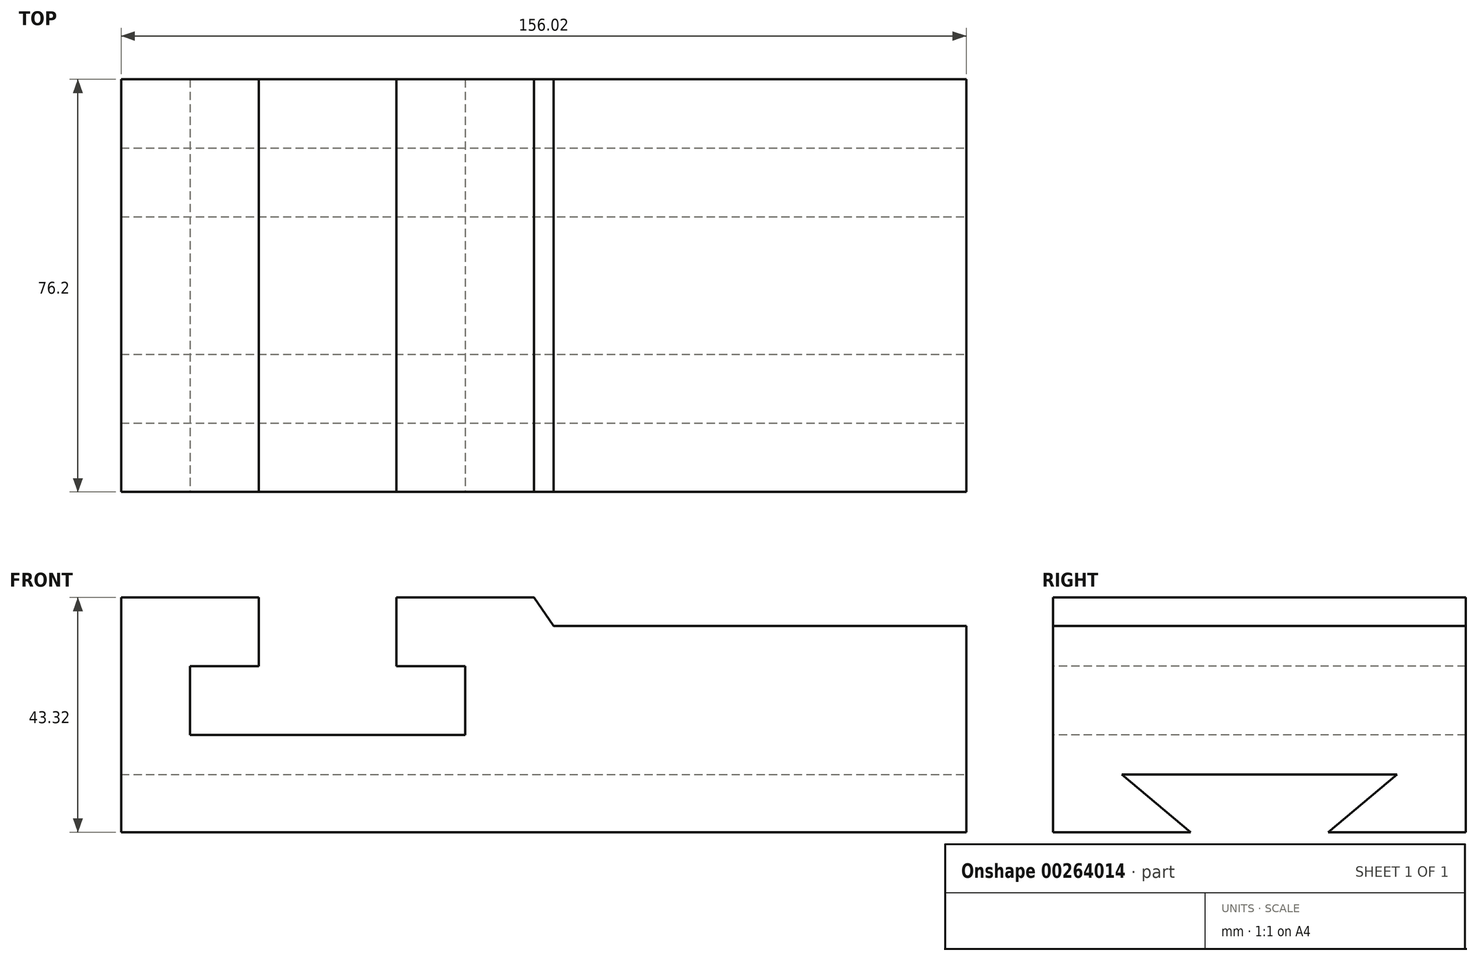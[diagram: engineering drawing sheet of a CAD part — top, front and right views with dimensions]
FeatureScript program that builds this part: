
annotation { "Feature Type Name" : "Feature", "Feature Type Description" : "" }
export const myFeature = defineFeature(function(context is Context, id is Id, definition is map)
    precondition{}
    {
        {
            var Q0;
            Q0=qCreatedBy(makeId("Front.planeOp"),FACE);
            var sketch = newSketch(context, id + "F0", { "sketchPlane" : qUnion([Q0])});
            skLineSegment(sketch, "E0", {"start": v(0, 0) * mm, "end": v(-76.2, 0) * mm});
            skLineSegment(sketch, "E1", {"start": v(0, 0) * mm, "end": v(76.2, 0) * mm});
            skLineSegment(sketch, "E2", {"start": v(76.2, 0) * mm, "end": v(76.2, 38.1) * mm});
            skLineSegment(sketch, "E3", {"start": v(76.2, 38.1) * mm, "end": v(0, 38.1) * mm});
            skLineSegment(sketch, "E4", {"start": v(0, 38.1) * mm, "end": v(-3.62, 43.32) * mm});
            skLineSegment(sketch, "E5", {"start": v(-3.62, 43.32) * mm, "end": v(-29.02, 43.32) * mm});
            skLineSegment(sketch, "E6", {"start": v(-29.02, 43.32) * mm, "end": v(-29.02, 30.62) * mm});
            skLineSegment(sketch, "E7", {"start": v(-29.02, 30.62) * mm, "end": v(-16.32, 30.62) * mm});
            skLineSegment(sketch, "E8", {"start": v(-16.32, 30.62) * mm, "end": v(-16.32, 17.92) * mm});
            skLineSegment(sketch, "E9", {"start": v(-16.32, 17.92) * mm, "end": v(-67.12, 17.92) * mm});
            skLineSegment(sketch, "E10", {"start": v(-67.12, 17.92) * mm, "end": v(-67.12, 30.62) * mm});
            skLineSegment(sketch, "E11", {"start": v(-67.12, 30.62) * mm, "end": v(-54.42, 30.62) * mm});
            skLineSegment(sketch, "E12", {"start": v(-54.42, 30.62) * mm, "end": v(-54.42, 43.32) * mm});
            skLineSegment(sketch, "E13", {"start": v(-54.42, 43.32) * mm, "end": v(-79.82, 43.32) * mm});
            skLineSegment(sketch, "E14", {"start": v(-79.82, 43.32) * mm, "end": v(-79.82, 0) * mm});
            skLineSegment(sketch, "E15", {"start": v(-79.82, 0) * mm, "end": v(-76.2, 0) * mm});
            skSolve(sketch);
        }
        {
            var Q0;
            Q0=makeQuery(id+"F0.imprint","IMPRINT",FACE,{"disambiguationData":[TD([[makeQuery(id+"F0.imprint","IMPRINT",EDGE,{"derivedFrom":sQuery(id+"F0.wireOp",EDGE,"E0")}),-1.0]])]});
            extrude(context, id + "F1", {"entities" : qUnion([Q0]), "oppositeDirection" : true, "depth" : 76.2 * mm});
        }
        {
            var Q0;
            Q0=makeQuery(id+"F1.opExtrude","SWEPT_FACE",FACE,{"disambiguationData":[OSD([sQuery(id+"F0.wireOp",EDGE,"E2")])]});
            var sketch = newSketch(context, id + "F2", { "sketchPlane" : qUnion([Q0])});
            skLineSegment(sketch, "E16", {"start": v(12.7, 10.65) * mm, "end": v(63.5, 10.65) * mm});
            skLineSegment(sketch, "E17", {"start": v(25.4, 0) * mm, "end": v(12.7, 10.65) * mm});
            skLineSegment(sketch, "E18", {"start": v(63.5, 10.65) * mm, "end": v(50.8, 0) * mm});
            skSolve(sketch);
        }
        {
            var Q0;
            Q0=makeQuery(id+"F2.imprint","IMPRINT",FACE,{"disambiguationData":[TD([[makeQuery(id+"F2.imprint","IMPRINT",EDGE,{"derivedFrom":sQuery(id+"F2.wireOp",EDGE,"E16")}),-1.0]])]});
            extrude(context, id + "F3", {"entities" : qUnion([Q0]), "operationType" : NewBodyOperationType.REMOVE, "endBound" : BoundingType.UP_TO_NEXT, "oppositeDirection" : true, "depth" : 25.4 * mm});
        }
    });
